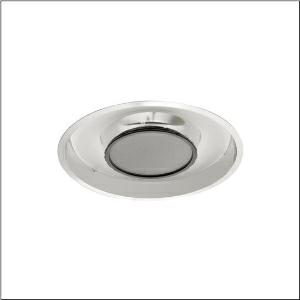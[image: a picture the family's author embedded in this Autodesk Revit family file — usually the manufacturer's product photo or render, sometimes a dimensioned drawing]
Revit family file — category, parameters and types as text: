
# Revit family: lunis_11_r_5lr610d4ob11af
name_source: partatom
category: Lighting Fixtures
units: mm (PartAtom-declared; Revit-internal decimal feet)

## family parameters
Cut with Voids When Loaded = No
Host = Face
Light Source = No
Part Type = Normal
Room Calculation Point = No
Round Connector Dimension = Use Diameter
Shared = No

## types (1)
- --- (1 x LED 4000K / CRI = 80 (unbekannt), 4860 lm, 4000K)
    Apparent Load = 37 VA
    CIE Flux Codes = 60 90 99 100 100
    Color Rendering = 80
    Color Temperature = 4000K
    Default Elevation = 1800 mm
    Description = Lunis 11 R, downlight, light control with reflector, of ultra-pure aluminium (Al 99.98%), highly specular, perforated, light emission: direct distribution, LED rated luminous flux: 4.860lm, light colour: 840, control gear: ECG Multilumen, with terminal, 3+2-pole, max. 2.5mm², mains connection: 230V, AC, 50/60Hz, diameter: 398mm, central ring, of plastic, graphite (RAL 7037), central module, blanking cover, of sheet steel, perforated, metallic grey (RAL 9006), protection rating (complete): IP20, insulation class (complete): insulation class II (safety insulation), certification: CE, ENEC, VDE, protection symbol: F, permissible ambient temperature for indoor applications: +10..+35°C, standard: EN 50419, packaging unit: 1 piece
    Height = 0 mm  [stored 0 ft]
    Lamp = 1 x LED 4000K / CRI >= 80 (unbekannt)
    Lamp Light Flux = 4860 lm
    Lamp count = 1
    Length = 398 mm
    Luminous efficacy = 131 lm/W
    Manufacturer = Siteco
    ModVariant = No
    Model = 5LR610D4OB11AF
    Mounting Place = Ceiling
    Mounting Type = Recessed
    Number of Poles = 1
    OnlyDefault = Yes
    Power Factor = 1
    Product Name = Lunis 11 R
    Product group = downlight
    ProductGroupID = 400
    Protection Class = Protection class II
    Protection Degree = IP 20
    RLX_Detail_Level = 1
    RLX_Emergency_Light_Flux = 0 lm
    RLX_Emergency_Type = 0
    RLX_Emergency_Type_DB = No
    RlxData = <blob elided: 94809 chars, md5=48e55fcc>
    Socket = socket
    Standby Power = 0 W
    System Light Flux = 4860 lm
    System Power = 37 W
    Type Comments = factory setting: High Lumen Output
    Type Image = l_1003323.jpg
    URL = http://relux.com
    VarID = @adj_148769
    Voltage = 0 V
    Weight = 0.00 kg
    Width = 0 mm  [stored 0 ft]

note: [stored X ft] marks values corroborated as IEEE doubles in the binary element streams (Revit-internal decimal feet)

## geometry (parser evidence)
native form markers: Blend x4, Sweep x12
no freeform markers — native parametric forms only
